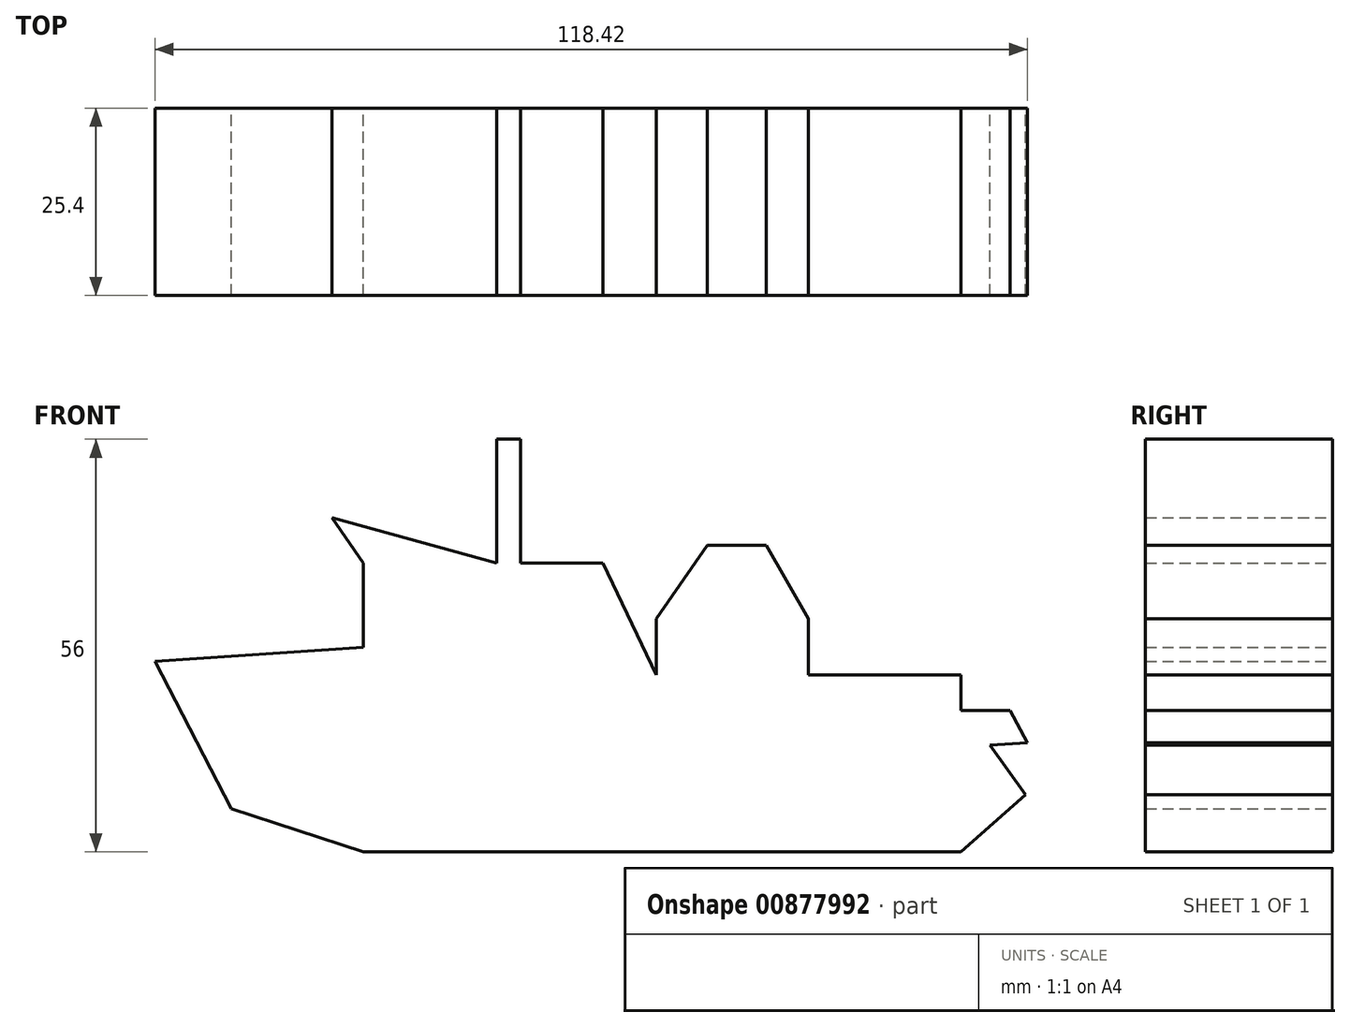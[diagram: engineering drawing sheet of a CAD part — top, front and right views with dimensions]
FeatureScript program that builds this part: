
annotation { "Feature Type Name" : "Feature", "Feature Type Description" : "" }
export const myFeature = defineFeature(function(context is Context, id is Id, definition is map)
    precondition{}
    {
        {
            var Q0;
            Q0=qCreatedBy(makeId("Front.planeOp"),FACE);
            var sketch = newSketch(context, id + "F0", { "sketchPlane" : qUnion([Q0])});
            skLineSegment(sketch, "E0", {"start": v(-60.8, 11.07) * mm, "end": v(-50.4, -8.94) * mm});
            skLineSegment(sketch, "E1", {"start": v(-50.4, -8.94) * mm, "end": v(-32.54, -14.8) * mm});
            skLineSegment(sketch, "E2", {"start": v(-32.54, -14.8) * mm, "end": v(17.07, -14.8) * mm});
            skLineSegment(sketch, "E3", {"start": v(17.07, -14.8) * mm, "end": v(48.54, -14.8) * mm});
            skLineSegment(sketch, "E4", {"start": v(48.54, -14.8) * mm, "end": v(48.54, 9.2) * mm});
            skLineSegment(sketch, "E5", {"start": v(48.54, 9.2) * mm, "end": v(7.2, 9.2) * mm});
            skLineSegment(sketch, "E6", {"start": v(7.2, 9.2) * mm, "end": v(0, 24.4) * mm});
            skLineSegment(sketch, "E7", {"start": v(0, 24.4) * mm, "end": v(-11.2, 24.4) * mm});
            skLineSegment(sketch, "E8", {"start": v(-11.2, 24.4) * mm, "end": v(-11.2, 41.2) * mm});
            skLineSegment(sketch, "E9", {"start": v(-11.2, 41.2) * mm, "end": v(-14.4, 41.2) * mm});
            skLineSegment(sketch, "E10", {"start": v(-14.4, 41.2) * mm, "end": v(-14.4, 24.4) * mm});
            skLineSegment(sketch, "E11", {"start": v(-14.4, 24.4) * mm, "end": v(-32.54, 24.4) * mm});
            skLineSegment(sketch, "E12", {"start": v(-32.54, 24.4) * mm, "end": v(-32.54, 12.93) * mm});
            skLineSegment(sketch, "E13", {"start": v(-32.54, 12.93) * mm, "end": v(-60.8, 11.07) * mm});
            skLineSegment(sketch, "E14", {"start": v(48.54, 4.4) * mm, "end": v(55.2, 4.4) * mm});
            skLineSegment(sketch, "E15", {"start": v(55.2, 4.4) * mm, "end": v(57.6, 0) * mm});
            skLineSegment(sketch, "E16", {"start": v(57.6, 0) * mm, "end": v(52.5, -0.34) * mm});
            skLineSegment(sketch, "E17", {"start": v(52.5, -0.34) * mm, "end": v(57.34, -7.07) * mm});
            skLineSegment(sketch, "E18", {"start": v(57.34, -7.07) * mm, "end": v(48.54, -14.8) * mm});
            skLineSegment(sketch, "E19", {"start": v(-32.54, 24.4) * mm, "end": v(-36.8, 30.53) * mm});
            skLineSegment(sketch, "E20", {"start": v(-36.8, 30.53) * mm, "end": v(-14.4, 24.4) * mm});
            skPoint(sketch, "E21.oppositeSnap0", {"position": v(27.87, 9.2) * mm});
            skPoint(sketch, "E21.oppositeSnap1", {"position": v(3.6, 16.8) * mm});
            skLineSegment(sketch, "E21.bottom", {"start": v(7.2, 9.2) * mm, "end": v(27.87, 9.2) * mm});
            skLineSegment(sketch, "E21.top", {"start": v(7.2, 16.8) * mm, "end": v(27.87, 16.8) * mm});
            skLineSegment(sketch, "E21.left", {"start": v(7.2, 9.2) * mm, "end": v(7.2, 16.8) * mm});
            skLineSegment(sketch, "E21.right", {"start": v(27.87, 9.2) * mm, "end": v(27.87, 16.8) * mm});
            skLineSegment(sketch, "E22", {"start": v(7.2, 16.8) * mm, "end": v(14.14, 26.8) * mm});
            skLineSegment(sketch, "E23", {"start": v(14.14, 26.8) * mm, "end": v(22.14, 26.8) * mm});
            skLineSegment(sketch, "E24", {"start": v(22.14, 26.8) * mm, "end": v(27.87, 16.8) * mm});
            skSolve(sketch);
        }
        {
            var Q0;
            Q0 = qSketchRegion(id + "F0", true);
            extrude(context, id + "F1", {"entities" : qUnion([Q0]), "depth" : 25.4 * mm, "offsetDistance" : 25.4 * mm});
        }
    });
